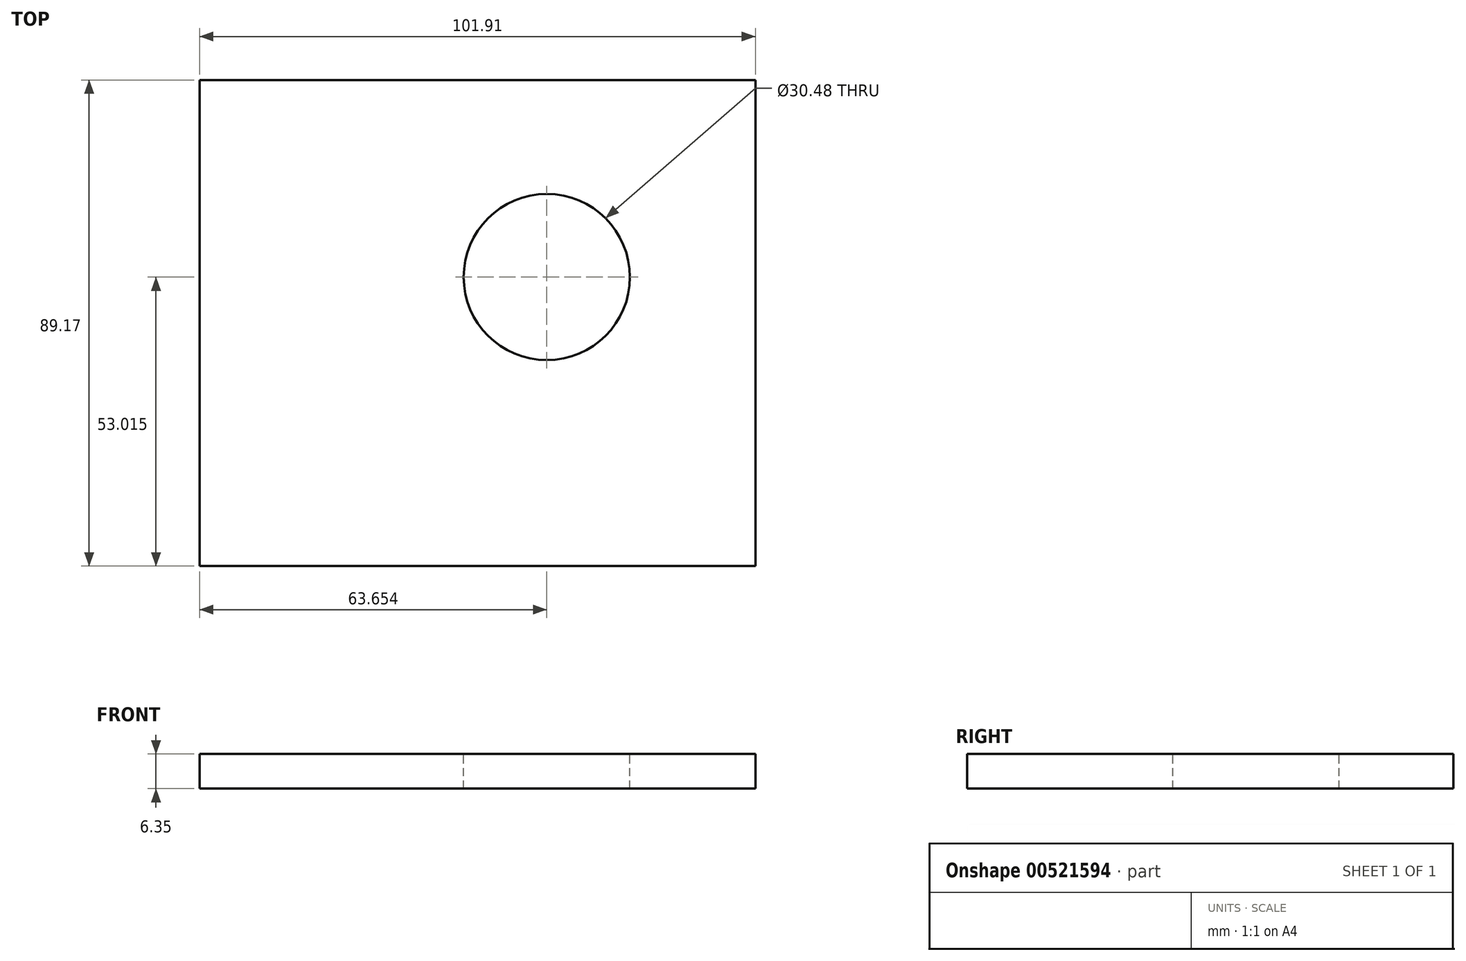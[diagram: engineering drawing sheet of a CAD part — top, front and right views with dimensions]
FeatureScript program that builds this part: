
annotation { "Feature Type Name" : "Feature", "Feature Type Description" : "" }
export const myFeature = defineFeature(function(context is Context, id is Id, definition is map)
    precondition{}
    {
        {
            var Q0;
            Q0=qCreatedBy(makeId("Top.planeOp"),FACE);
            var sketch = newSketch(context, id + "F0", { "sketchPlane" : qUnion([Q0])});
            skLineSegment(sketch, "E0.bottom", {"start": v(0, 0) * mm, "end": v(101.9, 0) * mm});
            skLineSegment(sketch, "E0.top", {"start": v(0, 89.17) * mm, "end": v(101.9, 89.17) * mm});
            skLineSegment(sketch, "E0.left", {"start": v(0, 0) * mm, "end": v(0, 89.17) * mm});
            skLineSegment(sketch, "E0.right", {"start": v(101.9, 0) * mm, "end": v(101.9, 89.17) * mm});
            skSolve(sketch);
        }
        {
            var Q0;
            Q0 = qSketchRegion(id + "F0", true);
            extrude(context, id + "F1", {"entities" : qUnion([Q0]), "depth" : 6.35 * mm, "offsetDistance" : 25.4 * mm});
        }
        {
            var Q0;
            Q0=makeQuery(id+"F1.opExtrude","CAP_FACE",FACE,{"disambiguationData":[OSD([sQuery(id+"F0.wireOp",EDGE,"E0.bottom"),sQuery(id+"F0.wireOp",EDGE,"E0.top"),sQuery(id+"F0.wireOp",EDGE,"E0.left"),sQuery(id+"F0.wireOp",EDGE,"E0.right")])],"isStart":false});
            var sketch = newSketch(context, id + "F2", { "sketchPlane" : qUnion([Q0])});
            skCircle(sketch, "E1", {"center": v(63.65, 53.01) * mm, "radius": 15.24 * mm});
            skSolve(sketch);
        }
        {
            var Q0;
            Q0 = qSketchRegion(id + "F2", true);
            extrude(context, id + "F3", {"entities" : qUnion([Q0]), "operationType" : NewBodyOperationType.REMOVE, "endBound" : BoundingType.UP_TO_NEXT, "oppositeDirection" : true, "depth" : 25.4 * mm, "offsetDistance" : 25.4 * mm});
        }
    });
